# Revit family: PRD_FrankeWS_PwrSpplUnts_PowerSupply_ZAQUA007,ZAQUA094
name_source: partatom
category: Electrical Equipment
revit_build: Autodesk Revit 2015 (Build: 20160512_1515(x64)
units: mm (PartAtom-declared; Revit-internal decimal feet)

## types (2) — shared parameters
AssetType = Fixed
Category = Pr_60_70, Power supply products
Description = Power supply - A3000 open in waterproof housing for wall mounting for supplying power to AQUA 3000 open fitting, 230 V AC / 24 V DC, 12 W.
DurationUnit = year
GrossWeight = 0.31 kg
IP_Code = IP68
IfcExportAs = IfcTransformerType
IfcExportType = NOTDEFINED
Manufacturer = FRANKE Water Systems AG
ManufacturerName = FRANKE Water Systems AG
ManufacturerURL = www.franke.com
MaximumApparentPower = 0 VA
NBSDescription = Power supply units
NBSReference = 90-70-05/390
NominalHeight = 43 mm  [stored 0.141076 ft]
NominalLength = 25 mm  [stored 0.082021 ft]
NominalWidth = 90 mm  [stored 0.295276 ft]
PowerSupplyMaterial = <By Category>
PrimaryApparentPower = 0 VA
PrimaryCurrent = 0 A
PrimaryFrequency = 50 Hz
PrimaryVoltage = 230 V
ProductInformation = http://igh.franke.mycontent.ch
SecondaryApparentPower = 0 VA
SecondaryCurrent = 0 A
SecondaryCurrentType = DC
SecondaryFrequency = 0 Hz
SecondaryVoltage = 24 V
Size = 90 x 43 x 25 mm
URL = www.franke.com
Uniclass2015Code = Pr_60_70
Uniclass2015Title = Power supply products
Uniclass2015Version = Products v1.7
Version = 1
Voltage = 230
WarrantyDurationUnit = year

## per-type parameters (varying)
| type | BIMObjectName | Model | ModelNumber | ModelReference | Name | NetWeight |
| ZAQUA007 - with standardised European plug | PRD_FrankeWS_PowerSupplyUnits_PowerSupply_ZAQUA007 | ZAQUA007 | 2000100375 | ZAQUA007 | Power supply ZAQUA007 | 0.24 kg |
| ZAQUA094 - with ferrules | PRD_FrankeWS_PowerSupplyUnits_PowerSupply_ZAQUA094 | ZAQUA094 | 2000102691 | ZAQUA094 | Power supply ZAQUA094 | 0.28 kg |

note: [stored X ft] marks values corroborated as IEEE doubles in the binary element streams (Revit-internal decimal feet)

## geometry (parser evidence)
native form markers: Sweep x3
no freeform markers — native parametric forms only
